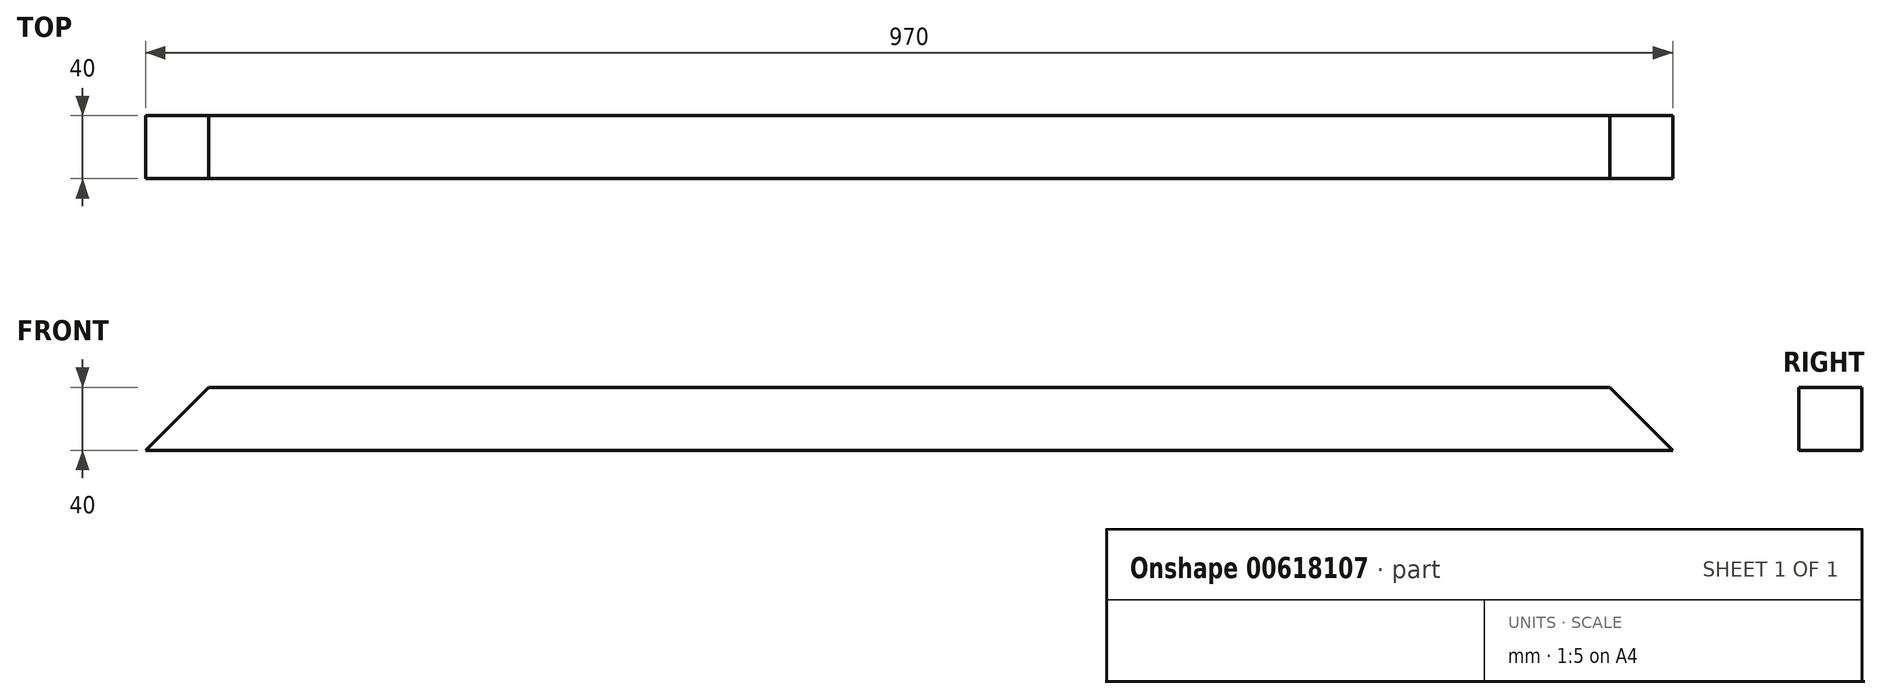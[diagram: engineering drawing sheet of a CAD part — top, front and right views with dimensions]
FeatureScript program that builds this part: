
annotation { "Feature Type Name" : "Feature", "Feature Type Description" : "" }
export const myFeature = defineFeature(function(context is Context, id is Id, definition is map)
    precondition{}
    {
        {
            var Q0;
            Q0=qCreatedBy(makeId("Front.planeOp"),FACE);
            var sketch = newSketch(context, id + "F0", { "sketchPlane" : qUnion([Q0])});
            skLineSegment(sketch, "E0.bottom", {"start": v(485, -20) * mm, "end": v(-485, -20) * mm});
            skLineSegment(sketch, "E0.top", {"start": v(445, 20) * mm, "end": v(-445, 20) * mm});
            skPoint(sketch, "E0.middle", {"position": v(0, 0) * mm});
            skLineSegment(sketch, "E1", {"start": v(-485, -20) * mm, "end": v(-445, 20) * mm});
            skLineSegment(sketch, "E2", {"start": v(445, 20) * mm, "end": v(485, -20) * mm});
            skPoint(sketch, "E3.end.orphan", {"position": v(445, -20) * mm});
            skSolve(sketch);
        }
        {
            var Q0;
            Q0 = qSketchRegion(id + "F0", true);
            extrude(context, id + "F1", {"entities" : qUnion([Q0]), "depth" : 40 * mm, "offsetDistance" : 25 * mm});
        }
    });
